annotation { "Feature Type Name" : "Feature", "Feature Type Description" : "" }
export const myFeature = defineFeature(function(context is Context, id is Id, definition is map)
    precondition{}
    {
        {
            var Q0;
            Q0=qCreatedBy(makeId("Top.planeOp"),FACE);
            var sketch = newSketch(context, id + "F0", { "sketchPlane" : qUnion([Q0])});
            skLineSegment(sketch, "E0.bottom", {"start": v(-44.45, 25.4) * mm, "end": v(44.45, 25.4) * mm});
            skLineSegment(sketch, "E0.top", {"start": v(-44.45, -25.4) * mm, "end": v(44.45, -25.4) * mm});
            skLineSegment(sketch, "E0.left", {"start": v(-44.45, 25.4) * mm, "end": v(-44.45, -25.4) * mm});
            skLineSegment(sketch, "E0.right", {"start": v(44.45, 25.4) * mm, "end": v(44.45, -25.4) * mm});
            skPoint(sketch, "E0.middle", {"position": v(0, 0) * mm});
            skSolve(sketch);
        }
        {
            var Q0;
            Q0=qSketchRegion(id+"F0",true);
            extrude(context, id + "F1", {"entities" : qUnion([Q0]), "depth" : 1.59 * mm, "offsetDistance" : 25.4 * mm});
        }
        {
            var Q0;
            {var subQ0=sQuery(id+"F0.wireOp",EDGE,"E0.right");var subQ1=sQuery(id+"F0.wireOp",EDGE,"E0.left");var subQ2=sQuery(id+"F0.wireOp",EDGE,"E0.top");var subQ3=sQuery(id+"F0.wireOp",EDGE,"E0.bottom");var subQ4=makeQuery(id+"F1.opExtrude","CAP_FACE",FACE,{"disambiguationData":[OSD([subQ3,subQ2,subQ1,subQ0])],"isStart":false});Q0=makeQuery(id+"F9.boolean.opBoolean","SPLIT",FACE,{"disambiguationData":[TD([makeQuery(id+"F5.boolean.opBoolean","COPY",FACE,{"derivedFrom":makeQuery(id+"F5.opExtrude","SWEPT_FACE",FACE,{"disambiguationData":[OSD([sQuery(id+"F4.wireOp",EDGE,"E32.sketch_text.stroke-0")])]})})])],"derivedFrom":subQ4});}
            var sketch = newSketch(context, id + "F2", { "sketchPlane" : qUnion([Q0])});
            skLineSegment(sketch, "E1", {"start": v(-39.93, 20.88) * mm, "end": v(-39.93, 13.23) * mm});
            skLineSegment(sketch, "E2", {"start": v(-39.93, 20.88) * mm, "end": v(-39.12, 20.88) * mm});
            skLineSegment(sketch, "E3", {"start": v(-37.79, -20.88) * mm, "end": v(-35.63, -20.88) * mm});
            skLineSegment(sketch, "E4.0", {"start": v(-11.09, 20.88) * mm, "end": v(-6.97, 18.68) * mm});
            skLineSegment(sketch, "E4.1", {"start": v(-14.12, 20.88) * mm, "end": v(-16.69, 18.68) * mm});
            skLineSegment(sketch, "E4.13", {"start": v(2.67, -20.88) * mm, "end": v(0.61, -18.26) * mm});
            skLineSegment(sketch, "E4.14", {"start": v(0.36, 11.02) * mm, "end": v(3.83, 4.92) * mm});
            skLineSegment(sketch, "E4.15", {"start": v(0.36, 11.02) * mm, "end": v(-4.42, 10.07) * mm});
            skArc(sketch, "E4.16", {"start": v(-4.42, 10.07) * mm, "mid": v(-5.98, 11.8) * mm, "end": v(-7.68, 13.38) * mm});
            skLineSegment(sketch, "E4.17", {"start": v(-6.97, 18.68) * mm, "end": v(-7.68, 13.38) * mm});
            skLineSegment(sketch, "E4.18", {"start": v(3.83, 4.92) * mm, "end": v(0.61, 1.3) * mm});
            skArc(sketch, "E4.19", {"start": v(1.92, -3.68) * mm, "mid": v(1.38, -1.16) * mm, "end": v(0.61, 1.3) * mm});
            skLineSegment(sketch, "E4.20", {"start": v(6.61, -5.16) * mm, "end": v(1.92, -3.68) * mm});
            skLineSegment(sketch, "E4.21", {"start": v(6.61, -5.16) * mm, "end": v(6.61, -11.77) * mm});
            skLineSegment(sketch, "E4.22", {"start": v(6.61, -11.77) * mm, "end": v(1.92, -13.28) * mm});
            skArc(sketch, "E4.23", {"start": v(0.61, -18.26) * mm, "mid": v(1.38, -15.8) * mm, "end": v(1.92, -13.28) * mm});
            skLineSegment(sketch, "E4.42", {"start": v(-39.12, 20.88) * mm, "end": v(-36.5, 18.68) * mm});
            skArc(sketch, "E4.43", {"start": v(-31.89, 19.94) * mm, "mid": v(-34.22, 19.4) * mm, "end": v(-36.5, 18.68) * mm});
            skLineSegment(sketch, "E4.44", {"start": v(-31.89, 19.94) * mm, "end": v(-31.5, 20.88) * mm});
            skLineSegment(sketch, "E4.46", {"start": v(-21.66, 20.88) * mm, "end": v(-21.3, 19.94) * mm});
            skArc(sketch, "E4.47", {"start": v(-16.69, 18.68) * mm, "mid": v(-18.96, 19.4) * mm, "end": v(-21.3, 19.94) * mm});
            skLineSegment(sketch, "E5.0", {"start": v(-17.63, -12.4) * mm, "end": v(-15.7, -16.29) * mm});
            skFitSpline(sketch, "E5.1", {"points": [v(-7.65, -15.55) * mm, v(-11.69, -15.5) * mm, v(-15.7, -16.29) * mm]});
            skLineSegment(sketch, "E5.2", {"start": v(-7.65, -15.55) * mm, "end": v(-7.5, -15.55) * mm});
            skLineSegment(sketch, "E5.3", {"start": v(-16.04, -3.68) * mm, "end": v(-14.6, -3.8) * mm});
            skFitSpline(sketch, "E5.4", {"points": [v(-14.36, -4.47) * mm, v(-14.33, -4.23) * mm, v(-14.32, -3.82) * mm, v(-14.6, -3.8) * mm]});
            skLineSegment(sketch, "E5.5", {"start": v(-14.36, -4.47) * mm, "end": v(-14.36, -7.44) * mm});
            skFitSpline(sketch, "E5.6", {"points": [v(-15.13, -7.93) * mm, v(-14.83, -7.99) * mm, v(-14.54, -8.08) * mm, v(-14.36, -7.44) * mm]});
            skFitSpline(sketch, "E5.7", {"points": [v(-16.04, -3.68) * mm, v(-16.1, 0.17) * mm, v(-19.42, 3.57) * mm, v(-23.98, 5.7) * mm, v(-24.16, 6.21) * mm]});
            skFitSpline(sketch, "E5.8", {"points": [v(-24.16, 6.21) * mm, v(-24.11, 7.19) * mm, v(-23.98, 11.28) * mm, v(-22.96, 13.3) * mm, v(-19.48, 14.97) * mm]});
            skFitSpline(sketch, "E5.9", {"points": [v(-19.48, 14.97) * mm, v(-20.81, 15.64) * mm, v(-22.46, 15.17) * mm]});
            skFitSpline(sketch, "E5.10", {"points": [v(-17.63, -12.4) * mm, v(-16.8, -10.89) * mm, v(-15.86, -9.46) * mm, v(-15.13, -7.93) * mm]});
            skFitSpline(sketch, "E5.11", {"points": [v(-22.46, 15.17) * mm, v(-21.72, 15.9) * mm, v(-20.87, 16.52) * mm]});
            skArc(sketch, "E5.12", {"start": v(-2.15, -17.45) * mm, "mid": v(-3.8, 3.8) * mm, "end": v(-20.87, 16.52) * mm});
            skLineSegment(sketch, "E5.13", {"start": v(-7.5, -15.55) * mm, "end": v(-2.15, -17.45) * mm});
            skArc(sketch, "E6.0", {"start": v(-31.1, 16.66) * mm, "mid": v(-35.68, 15.36) * mm, "end": v(-39.93, 13.23) * mm});
            skLineSegment(sketch, "E6.2", {"start": v(-38.12, -3.8) * mm, "end": v(-37.08, -3.8) * mm});
            skFitSpline(sketch, "E6.3", {"points": [v(-29.04, 5.91) * mm, v(-32.6, 3.54) * mm, v(-36.03, 3.27) * mm, v(-37.08, -3.8) * mm]});
            skFitSpline(sketch, "E6.4", {"points": [v(-32.5, 12.72) * mm, v(-29.26, 10.64) * mm, v(-29.04, 5.91) * mm]});
            skFitSpline(sketch, "E6.5", {"points": [v(-29.6, 12.07) * mm, v(-30.83, 12.9) * mm, v(-32.5, 12.72) * mm]});
            skFitSpline(sketch, "E6.6", {"points": [v(-38.12, -3.8) * mm, v(-38.46, -3.77) * mm, v(-38.6, -3.99) * mm, v(-38.6, -4.15) * mm]});
            skLineSegment(sketch, "E6.7", {"start": v(-38.6, -7.34) * mm, "end": v(-38.6, -4.15) * mm});
            skFitSpline(sketch, "E6.8", {"points": [v(-31.1, 16.66) * mm, v(-30.26, 15.3) * mm, v(-29.66, 13.77) * mm, v(-29.6, 12.07) * mm]});
            skFitSpline(sketch, "E6.9", {"points": [v(-38.6, -7.34) * mm, v(-38.84, -7.76) * mm, v(-38.04, -8) * mm]});
            skFitSpline(sketch, "E6.10", {"points": [v(-38.04, -8) * mm, v(-36.8, -10.21) * mm, v(-35.5, -12.4) * mm]});
            skLineSegment(sketch, "E6.11", {"start": v(-37.39, -16.29) * mm, "end": v(-35.5, -12.4) * mm});
            skFitSpline(sketch, "E6.12", {"points": [v(-37.39, -16.29) * mm, v(-41.55, -15.61) * mm, v(-45.73, -15.55) * mm]});
            skLineSegment(sketch, "E7.0", {"start": v(-33.08, -20.88) * mm, "end": v(-35.5, -19.2) * mm});
            skLineSegment(sketch, "E7.1", {"start": v(-35.5, -19.2) * mm, "end": v(-35.63, -20.88) * mm});
            skArc(sketch, "E8.1", {"start": v(-3.7, -20.88) * mm, "mid": v(-3.07, -19.66) * mm, "end": v(-2.52, -18.4) * mm});
            skLineSegment(sketch, "E8.2", {"start": v(-16.04, -18.26) * mm, "end": v(-15.47, -20.88) * mm});
            skFitSpline(sketch, "E8.3", {"points": [v(-16.04, -18.26) * mm, v(-16.15, -17.79) * mm, v(-15.43, -17.5) * mm]});
            skLineSegment(sketch, "E8.4", {"start": v(-7.5, -16.6) * mm, "end": v(-15.43, -17.5) * mm});
            skLineSegment(sketch, "E8.6", {"start": v(-2.52, -18.4) * mm, "end": v(-7.5, -16.6) * mm});
            skLineSegment(sketch, "E9.0", {"start": v(-37.39, -17.54) * mm, "end": v(-39.93, -17.25) * mm});
            skLineSegment(sketch, "E9.1", {"start": v(-37.79, -20.88) * mm, "end": v(-37.39, -18.92) * mm});
            skFitSpline(sketch, "E9.3", {"points": [v(-37.39, -17.54) * mm, v(-37.1, -18.3) * mm, v(-37.39, -18.92) * mm]});
            skFitSpline(sketch, "E10.0", {"points": [v(-23.19, -19.91) * mm, v(-20.18, -18.37) * mm, v(-17.6, -16.11) * mm]});
            skFitSpline(sketch, "E10.1", {"points": [v(-23.19, -19.91) * mm, v(-23.5, -19.6) * mm, v(-23.9, -19.16) * mm, v(-24.45, -18.66) * mm]});
            skFitSpline(sketch, "E10.2", {"points": [v(-17.6, -16.11) * mm, v(-17.44, -16.44) * mm, v(-17.63, -16.6) * mm]});
            skFitSpline(sketch, "E10.3", {"points": [v(-18.7, -14.2) * mm, v(-21.24, -16.8) * mm, v(-24.45, -18.66) * mm]});
            skLineSegment(sketch, "E10.4", {"start": v(-18.7, -14.2) * mm, "end": v(-18.94, -13.74) * mm});
            skFitSpline(sketch, "E10.5", {"points": [v(-17.63, -16.6) * mm, v(-19.85, -19.09) * mm, v(-22.95, -21.46) * mm, v(-27.12, -22.28) * mm, v(-31.04, -20.92) * mm, v(-33.86, -17.94) * mm, v(-35.78, -16.6) * mm]});
            skLineSegment(sketch, "E10.6", {"start": v(-34.7, -13.28) * mm, "end": v(-35.78, -16.6) * mm});
            skFitSpline(sketch, "E10.7", {"points": [v(-26.6, -18.92) * mm, v(-31.06, -16.8) * mm, v(-34.7, -13.28) * mm]});
            skFitSpline(sketch, "E10.8", {"points": [v(-18.94, -13.74) * mm, v(-21.29, -15.73) * mm, v(-23.66, -17.85) * mm, v(-26.6, -18.92) * mm]});
            skFitSpline(sketch, "E11.0", {"points": [v(-26.6, -17.54) * mm, v(-28.47, -16.2) * mm, v(-32.14, -14.27) * mm, v(-34.18, -11.66) * mm, v(-36.38, -8.05) * mm, v(-36.5, -7.34) * mm]});
            skLineSegment(sketch, "E11.1", {"start": v(-26.6, -17.54) * mm, "end": v(-24.45, -16.29) * mm});
            skFitSpline(sketch, "E11.2", {"points": [v(-26.34, -3.1) * mm, v(-21.2, -4.73) * mm, v(-16.46, -7.44) * mm]});
            skFitSpline(sketch, "E11.3", {"points": [v(-16.46, -7.44) * mm, v(-17.65, -7.44) * mm, v(-21.16, -6.55) * mm, v(-24.06, -4.55) * mm, v(-26.56, -4.47) * mm]});
            skLineSegment(sketch, "E11.4", {"start": v(-26.56, -11.18) * mm, "end": v(-26.56, -4.47) * mm});
            skFitSpline(sketch, "E11.5", {"points": [v(-36.5, -7.34) * mm, v(-33.28, -5.58) * mm, v(-29.94, -4) * mm, v(-26.34, -3.1) * mm]});
            skFitSpline(sketch, "E11.6", {"points": [v(-26.56, -11.18) * mm, v(-25.5, -14.07) * mm, v(-26.07, -15.95) * mm, v(-24.45, -16.29) * mm]});
            skFitSpline(sketch, "E12.0", {"points": [v(-29.8, -6.2) * mm, v(-28.78, -9.6) * mm, v(-28.81, -13.06) * mm]});
            skLineSegment(sketch, "E12.1", {"start": v(-28.45, -5.16) * mm, "end": v(-29.8, -6.2) * mm});
            skFitSpline(sketch, "E12.2", {"points": [v(-28.17, -12.77) * mm, v(-28.23, -8.96) * mm, v(-28.45, -5.16) * mm]});
            skFitSpline(sketch, "E12.3", {"points": [v(-28.81, -13.06) * mm, v(-28.3, -13.1) * mm, v(-28.17, -12.77) * mm]});
            skFitSpline(sketch, "E13.0", {"points": [v(-31.61, -12.77) * mm, v(-31.3, -12.82) * mm, v(-31.1, -12.4) * mm]});
            skFitSpline(sketch, "E13.1", {"points": [v(-32.64, -7.63) * mm, v(-31.76, -10.15) * mm, v(-31.61, -12.77) * mm]});
            skLineSegment(sketch, "E13.2", {"start": v(-31.61, -6.96) * mm, "end": v(-32.64, -7.63) * mm});
            skFitSpline(sketch, "E13.3", {"points": [v(-31.1, -12.4) * mm, v(-31.28, -9.67) * mm, v(-31.61, -6.96) * mm]});
            skFitSpline(sketch, "E14.0", {"points": [v(-25, -12.77) * mm, v(-24.92, -13.1) * mm, v(-24.52, -13.36) * mm, v(-23.99, -13.06) * mm]});
            skFitSpline(sketch, "E14.1", {"points": [v(-25, -12.77) * mm, v(-25.05, -9.05) * mm, v(-24.8, -5.34) * mm]});
            skLineSegment(sketch, "E14.2", {"start": v(-23.19, -6.2) * mm, "end": v(-24.8, -5.34) * mm});
            skFitSpline(sketch, "E14.3", {"points": [v(-23.99, -13.06) * mm, v(-24.35, -9.62) * mm, v(-23.19, -6.2) * mm]});
            skFitSpline(sketch, "E15.0", {"points": [v(-21.3, -12.77) * mm, v(-21.41, -12.73) * mm, v(-21.9, -12.9) * mm, v(-22.07, -12.52) * mm]});
            skFitSpline(sketch, "E15.1", {"points": [v(-21.3, -12.77) * mm, v(-21.22, -10.15) * mm, v(-20.3, -7.63) * mm]});
            skLineSegment(sketch, "E15.2", {"start": v(-20.3, -7.63) * mm, "end": v(-21.64, -6.96) * mm});
            skFitSpline(sketch, "E15.3", {"points": [v(-22.07, -12.52) * mm, v(-21.76, -9.75) * mm, v(-21.64, -6.96) * mm]});
            skFitSpline(sketch, "E16.0", {"points": [v(-27.86, -2.82) * mm, v(-31.79, -3.78) * mm, v(-35.38, -5.78) * mm]});
            skLineSegment(sketch, "E16.1", {"start": v(-27.86, -2.82) * mm, "end": v(-27.44, -1.99) * mm});
            skFitSpline(sketch, "E16.2", {"points": [v(-27.44, -1.99) * mm, v(-31.46, -2.27) * mm, v(-35.22, -4.15) * mm]});
            skFitSpline(sketch, "E16.3", {"points": [v(-35.38, -5.78) * mm, v(-35.64, -4.85) * mm, v(-35.22, -4.15) * mm]});
            skFitSpline(sketch, "E17.0", {"points": [v(-25.24, -2.82) * mm, v(-21.38, -3.85) * mm, v(-17.74, -5.62) * mm]});
            skLineSegment(sketch, "E17.1", {"start": v(-25.46, -1.99) * mm, "end": v(-25.24, -2.82) * mm});
            skFitSpline(sketch, "E17.2", {"points": [v(-17.63, -4.47) * mm, v(-21.2, -2.44) * mm, v(-25.46, -1.99) * mm]});
            skFitSpline(sketch, "E17.3", {"points": [v(-17.74, -5.62) * mm, v(-17.54, -5.08) * mm, v(-17.63, -4.47) * mm]});
            skLineSegment(sketch, "E18.0", {"start": v(-21.64, 16.53) * mm, "end": v(-21.52, 16.66) * mm});
            skArc(sketch, "E18.1", {"start": v(-21.52, 16.66) * mm, "mid": v(-22.69, 16.85) * mm, "end": v(-23.87, 17) * mm});
            skLineSegment(sketch, "E18.2", {"start": v(-23.87, 17) * mm, "end": v(-26.6, 10.84) * mm});
            skLineSegment(sketch, "E18.3", {"start": v(-26.6, 10.84) * mm, "end": v(-26.6, 17.1) * mm});
            skArc(sketch, "E18.4", {"start": v(-26.6, 17.1) * mm, "mid": v(-27.38, 17.09) * mm, "end": v(-28.17, 17.04) * mm});
            skFitSpline(sketch, "E18.5", {"points": [v(-21.64, 16.53) * mm, v(-22.97, 15.4) * mm, v(-23.04, 15.44) * mm, v(-23.74, 14.42) * mm, v(-23.43, 14.3) * mm]});
            skLineSegment(sketch, "E18.6", {"start": v(-28.17, 17.04) * mm, "end": v(-27.72, 12.88) * mm});
            skLineSegment(sketch, "E18.7", {"start": v(-26.6, 9.5) * mm, "end": v(-24.6, 6.5) * mm});
            skFitSpline(sketch, "E18.8", {"points": [v(-20.66, 14.78) * mm, v(-22.53, 14.03) * mm, v(-23.6, 12.91) * mm, v(-24.83, 10.42) * mm, v(-24.5, 8.42) * mm, v(-24.6, 6.5) * mm]});
            skFitSpline(sketch, "E18.9", {"points": [v(-23.39, 14.3) * mm, v(-22.04, 14.87) * mm, v(-20.66, 14.78) * mm]});
            skLineSegment(sketch, "E18.10", {"start": v(-23.39, 14.3) * mm, "end": v(-23.43, 14.3) * mm});
            skLineSegment(sketch, "E18.11", {"start": v(-28.64, 6.21) * mm, "end": v(-26.6, 9.5) * mm});
            skFitSpline(sketch, "E18.12", {"points": [v(-28.64, 6.21) * mm, v(-28.74, 9.43) * mm, v(-31.1, 12.15) * mm]});
            skFitSpline(sketch, "E18.13", {"points": [v(-31.1, 12.15) * mm, v(-30.03, 12.01) * mm, v(-29.04, 11.5) * mm]});
            skFitSpline(sketch, "E18.14", {"points": [v(-29.04, 11.5) * mm, v(-29.32, 14.22) * mm, v(-30.54, 16.77) * mm]});
            skArc(sketch, "E18.15", {"start": v(-29.04, 16.97) * mm, "mid": v(-29.79, 16.88) * mm, "end": v(-30.54, 16.77) * mm});
            skLineSegment(sketch, "E18.16", {"start": v(-27.72, 12.88) * mm, "end": v(-29.04, 16.97) * mm});
            skFitSpline(sketch, "E19.0", {"points": [v(-35.78, -3.1) * mm, v(-35.06, 1.3) * mm, v(-31.74, 3.25) * mm, v(-28.45, 4.52) * mm]});
            skFitSpline(sketch, "E20.0", {"points": [v(-28.45, 4.52) * mm, v(-27.52, 5.12) * mm, v(-27.11, 6.28) * mm, v(-26.6, 7.24) * mm]});
            skFitSpline(sketch, "E21.0", {"points": [v(-25.15, 4.92) * mm, v(-21.92, 3.09) * mm, v(-16.98, 0.88) * mm, v(-17.42, -3.1) * mm]});
            skFitSpline(sketch, "E21.1", {"points": [v(-26.6, 7.24) * mm, v(-25.96, 6.59) * mm, v(-25.67, 5.71) * mm, v(-25.15, 4.92) * mm]});
            skFitSpline(sketch, "E22.0", {"points": [v(-35.78, -3.1) * mm, v(-32.32, -2.55) * mm, v(-26.97, 0.08) * mm, v(-20.8, -2.33) * mm, v(-17.42, -3.1) * mm]});
            skLineSegment(sketch, "E23.trimOffspring", {"start": v(-39.93, -15.93) * mm, "end": v(-39.93, -17.25) * mm});
            skLineSegment(sketch, "E24.trimOffspring", {"start": v(-33.08, -20.88) * mm, "end": v(-30.2, -20.88) * mm});
            skFitSpline(sketch, "E25.trimOffspring", {"points": [v(-17.63, -16.6) * mm, v(-19.85, -19.09) * mm, v(-22.95, -21.46) * mm, v(-27.12, -22.28) * mm, v(-31.04, -20.92) * mm, v(-33.86, -17.94) * mm, v(-35.78, -16.6) * mm]});
            skLineSegment(sketch, "E26.trimOffspring", {"start": v(-22.9, -20.88) * mm, "end": v(-15.47, -20.88) * mm});
            skLineSegment(sketch, "E27.trimOffspring", {"start": v(-3.7, -20.88) * mm, "end": v(2.67, -20.88) * mm});
            skPoint(sketch, "E28.orphan", {"position": v(87.07, -20.88) * mm});
            skLineSegment(sketch, "E29.trimOffspring", {"start": v(-31.5, 20.88) * mm, "end": v(-21.66, 20.88) * mm});
            skPoint(sketch, "E30.orphan", {"position": v(48.02, 20.88) * mm});
            skLineSegment(sketch, "E31.trimOffspring", {"start": v(-14.12, 20.88) * mm, "end": v(-11.09, 20.88) * mm});
            skSolve(sketch);
        }
        {
            var Q0;
            Q0=qSketchRegion(id+"F2",true);
            extrude(context, id + "F3", {"entities" : qUnion([Q0]), "operationType" : NewBodyOperationType.ADD, "depth" : 0.8 * mm, "offsetDistance" : 25.4 * mm});
        }
        {
            var Q0;
            Q0=makeQuery(id+"F1.opExtrude","CAP_FACE",FACE,{"disambiguationData":[OSD([sQuery(id+"F0.wireOp",EDGE,"E0.bottom"),sQuery(id+"F0.wireOp",EDGE,"E0.top"),sQuery(id+"F0.wireOp",EDGE,"E0.left"),sQuery(id+"F0.wireOp",EDGE,"E0.right")])],"isStart":false});
            var sketch = newSketch(context, id + "F4", { "sketchPlane" : qUnion([Q0])});
            skText(sketch, "E32", { "text": "Josh Heger", "fontName": "AllertaStencil-Regular.ttf"});
            skText(sketch, "E33", { "text": "Human Player", "fontName": "AllertaStencil-Regular.ttf"});
            skText(sketch, "E34", { "text": "Team 501", "fontName": "AllertaStencil-Regular.ttf"});
            skPoint(sketch, "E35", {"position": v(0, 2.54) * mm});
            skPoint(sketch, "E36", {"position": v(0, 0) * mm});
            const initialGuessF4  = {"E32": [-0.03937, 0.0127, 1, 0, 0.00762], "E33": [-0.00956, 0.00508, 1, 0, 0.00508], "E34": [-0.01668, -0.00254, 1, 0, 0.00508]};
            skSetInitialGuess(sketch, initialGuessF4);
            skSolve(sketch);
        }
        {
            var Q0;
            Q0=qSketchRegion(id+"F4",true);
            extrude(context, id + "F5", {"entities" : qUnion([Q0]), "operationType" : NewBodyOperationType.REMOVE, "oppositeDirection" : true, "depth" : 1 / 812.8 * mm, "offsetDistance" : 25.4 * mm, "hasSecondDirection" : true, "secondDirectionOppositeDirection" : false, "secondDirectionDepth" : 25.4 * mm});
        }
        {
            var Q0;
            Q0=makeQuery(id+"F1.opExtrude","SWEPT_EDGE",EDGE,{"disambiguationData":[OSD([sQuery(id+"F0.wireOp",EDGE,"E0.bottom"),sQuery(id+"F0.wireOp",EDGE,"E0.left")])]});
            var Q1;
            Q1=makeQuery(id+"F1.opExtrude","SWEPT_EDGE",EDGE,{"disambiguationData":[OSD([sQuery(id+"F0.wireOp",EDGE,"E0.bottom"),sQuery(id+"F0.wireOp",EDGE,"E0.right")])]});
            var Q2;
            Q2=makeQuery(id+"F1.opExtrude","SWEPT_EDGE",EDGE,{"disambiguationData":[OSD([sQuery(id+"F0.wireOp",EDGE,"E0.top"),sQuery(id+"F0.wireOp",EDGE,"E0.right")])]});
            var Q3;
            Q3=makeQuery(id+"F1.opExtrude","SWEPT_EDGE",EDGE,{"disambiguationData":[OSD([sQuery(id+"F0.wireOp",EDGE,"E0.top"),sQuery(id+"F0.wireOp",EDGE,"E0.left")])]});
            fillet(context, id + "F6", {"entities" : qUnion([Q0, Q1, Q2, Q3]), "radius" : 5.08 * mm, "tangentPropagation" : true, "allowEdgeOverflow" : false});
        }
        {
            var Q0;
            Q0=makeQuery(id+"F1.opExtrude","CAP_EDGE",EDGE,{"disambiguationData":[OSD([sQuery(id+"F0.wireOp",EDGE,"E0.bottom")])],"isStart":false});
            fillet(context, id + "F7", {"entities" : qUnion([Q0]), "radius" : 5.08 * mm, "tangentPropagation" : true, "allowEdgeOverflow" : false});
        }
        {
            var Q0;
            Q0=makeQuery(id+"F1.opExtrude","CAP_FACE",FACE,{"disambiguationData":[OSD([sQuery(id+"F0.wireOp",EDGE,"E0.bottom"),sQuery(id+"F0.wireOp",EDGE,"E0.top"),sQuery(id+"F0.wireOp",EDGE,"E0.left"),sQuery(id+"F0.wireOp",EDGE,"E0.right")])],"isStart":false});
            var sketch = newSketch(context, id + "F8", { "sketchPlane" : qUnion([Q0])});
            skLineSegment(sketch, "E37", {"start": v(36.7, -11.99) * mm, "end": v(36.7, -7.33) * mm});
            skLineSegment(sketch, "E38", {"start": v(33.74, -7.33) * mm, "end": v(33.74, -10.97) * mm});
            skLineSegment(sketch, "E39", {"start": v(32.73, -11.99) * mm, "end": v(32.43, -11.99) * mm});
            skLineSegment(sketch, "E40", {"start": v(31.41, -10.97) * mm, "end": v(31.41, -7.33) * mm});
            skLineSegment(sketch, "E41", {"start": v(28.45, -7.33) * mm, "end": v(28.45, -10.97) * mm});
            skLineSegment(sketch, "E42", {"start": v(27.44, -11.99) * mm, "end": v(27.14, -11.99) * mm});
            skLineSegment(sketch, "E43", {"start": v(26.12, -10.97) * mm, "end": v(26.12, -7.33) * mm});
            skLineSegment(sketch, "E44", {"start": v(25.1, -6.31) * mm, "end": v(24.18, -6.31) * mm});
            skLineSegment(sketch, "E45", {"start": v(23.16, -7.33) * mm, "end": v(23.16, -10.97) * mm});
            skLineSegment(sketch, "E46", {"start": v(22.14, -11.99) * mm, "end": v(21.85, -11.99) * mm});
            skLineSegment(sketch, "E47", {"start": v(20.83, -10.97) * mm, "end": v(20.83, -7.33) * mm});
            skLineSegment(sketch, "E48", {"start": v(19.82, -6.31) * mm, "end": v(18.88, -6.31) * mm});
            skLineSegment(sketch, "E49", {"start": v(17.87, -7.33) * mm, "end": v(17.87, -10.97) * mm});
            skLineSegment(sketch, "E50", {"start": v(16.85, -11.99) * mm, "end": v(16.56, -11.99) * mm});
            skLineSegment(sketch, "E51", {"start": v(15.54, -10.97) * mm, "end": v(15.54, -7.33) * mm});
            skLineSegment(sketch, "E52", {"start": v(14.52, -6.31) * mm, "end": v(13.6, -6.31) * mm});
            skLineSegment(sketch, "E53", {"start": v(12.58, -7.33) * mm, "end": v(12.58, -11.99) * mm});
            skLineSegment(sketch, "E54", {"start": v(36.7, -11.99) * mm, "end": v(36.7, -17.66) * mm});
            skLineSegment(sketch, "E55", {"start": v(36.7, -17.66) * mm, "end": v(12.58, -17.66) * mm});
            skLineSegment(sketch, "E56", {"start": v(12.58, -17.66) * mm, "end": v(12.58, -11.99) * mm});
            skLineSegment(sketch, "E57", {"start": v(35.7, -6.31) * mm, "end": v(34.76, -6.31) * mm});
            skLineSegment(sketch, "E58", {"start": v(30.4, -6.31) * mm, "end": v(29.47, -6.31) * mm});
            skLineSegment(sketch, "E59", {"start": v(-40, -91.08) * mm, "end": v(-33.35, -89.42) * mm});
            skPoint(sketch, "E60.visualSharp", {"position": v(36.7, -6.31) * mm});
            skArc(sketch, "E60.filletArc", {"start": v(36.7, -7.33) * mm, "mid": v(36.4, -6.61) * mm, "end": v(35.7, -6.31) * mm});
            skPoint(sketch, "E61.visualSharp", {"position": v(33.74, -6.31) * mm});
            skArc(sketch, "E61.filletArc", {"start": v(34.76, -6.31) * mm, "mid": v(34.04, -6.61) * mm, "end": v(33.74, -7.33) * mm});
            skPoint(sketch, "E62.visualSharp", {"position": v(33.74, -11.99) * mm});
            skArc(sketch, "E62.filletArc", {"start": v(32.73, -11.99) * mm, "mid": v(33.45, -11.69) * mm, "end": v(33.74, -10.97) * mm});
            skPoint(sketch, "E63.visualSharp", {"position": v(31.41, -11.99) * mm});
            skArc(sketch, "E63.filletArc", {"start": v(31.41, -10.97) * mm, "mid": v(31.71, -11.69) * mm, "end": v(32.43, -11.99) * mm});
            skPoint(sketch, "E64.visualSharp", {"position": v(31.41, -6.31) * mm});
            skArc(sketch, "E64.filletArc", {"start": v(31.41, -7.33) * mm, "mid": v(31.12, -6.61) * mm, "end": v(30.4, -6.31) * mm});
            skPoint(sketch, "E65.visualSharp", {"position": v(28.45, -6.31) * mm});
            skArc(sketch, "E65.filletArc", {"start": v(29.47, -6.31) * mm, "mid": v(28.75, -6.61) * mm, "end": v(28.45, -7.33) * mm});
            skPoint(sketch, "E66.visualSharp", {"position": v(28.45, -11.99) * mm});
            skArc(sketch, "E66.filletArc", {"start": v(27.44, -11.99) * mm, "mid": v(28.15, -11.69) * mm, "end": v(28.45, -10.97) * mm});
            skPoint(sketch, "E67.visualSharp", {"position": v(26.12, -11.99) * mm});
            skArc(sketch, "E67.filletArc", {"start": v(26.12, -10.97) * mm, "mid": v(26.42, -11.69) * mm, "end": v(27.14, -11.99) * mm});
            skPoint(sketch, "E68.visualSharp", {"position": v(26.12, -6.31) * mm});
            skArc(sketch, "E68.filletArc", {"start": v(26.12, -7.33) * mm, "mid": v(25.83, -6.61) * mm, "end": v(25.1, -6.31) * mm});
            skPoint(sketch, "E69.visualSharp", {"position": v(23.16, -6.31) * mm});
            skArc(sketch, "E69.filletArc", {"start": v(24.18, -6.31) * mm, "mid": v(23.46, -6.61) * mm, "end": v(23.16, -7.33) * mm});
            skPoint(sketch, "E70.visualSharp", {"position": v(23.16, -11.99) * mm});
            skArc(sketch, "E70.filletArc", {"start": v(22.14, -11.99) * mm, "mid": v(22.86, -11.69) * mm, "end": v(23.16, -10.97) * mm});
            skPoint(sketch, "E71.visualSharp", {"position": v(20.83, -11.99) * mm});
            skArc(sketch, "E71.filletArc", {"start": v(20.83, -10.97) * mm, "mid": v(21.13, -11.69) * mm, "end": v(21.85, -11.99) * mm});
            skPoint(sketch, "E72.visualSharp", {"position": v(20.83, -6.31) * mm});
            skArc(sketch, "E72.filletArc", {"start": v(20.83, -7.33) * mm, "mid": v(20.53, -6.61) * mm, "end": v(19.82, -6.31) * mm});
            skPoint(sketch, "E73.visualSharp", {"position": v(17.87, -6.31) * mm});
            skArc(sketch, "E73.filletArc", {"start": v(18.88, -6.31) * mm, "mid": v(18.17, -6.61) * mm, "end": v(17.87, -7.33) * mm});
            skPoint(sketch, "E74.visualSharp", {"position": v(15.54, -6.31) * mm});
            skArc(sketch, "E74.filletArc", {"start": v(15.54, -7.33) * mm, "mid": v(15.24, -6.61) * mm, "end": v(14.52, -6.31) * mm});
            skPoint(sketch, "E75.visualSharp", {"position": v(15.54, -11.99) * mm});
            skArc(sketch, "E75.filletArc", {"start": v(15.54, -10.97) * mm, "mid": v(15.84, -11.69) * mm, "end": v(16.56, -11.99) * mm});
            skPoint(sketch, "E76.visualSharp", {"position": v(17.87, -11.99) * mm});
            skArc(sketch, "E76.filletArc", {"start": v(16.85, -11.99) * mm, "mid": v(17.57, -11.69) * mm, "end": v(17.87, -10.97) * mm});
            skPoint(sketch, "E77.visualSharp", {"position": v(12.58, -6.31) * mm});
            skArc(sketch, "E77.filletArc", {"start": v(13.6, -6.31) * mm, "mid": v(12.87, -6.61) * mm, "end": v(12.58, -7.33) * mm});
            skLineSegment(sketch, "E78.bottom", {"start": v(11.3, -20.2) * mm, "end": v(37.98, -20.2) * mm});
            skLineSegment(sketch, "E78.top", {"start": v(11.3, -3.77) * mm, "end": v(37.98, -3.77) * mm});
            skLineSegment(sketch, "E78.left", {"start": v(11.3, -20.2) * mm, "end": v(11.3, -3.77) * mm});
            skLineSegment(sketch, "E78.right", {"start": v(37.98, -20.2) * mm, "end": v(37.98, -3.77) * mm});
            skLineSegment(sketch, "E79.0", {"start": v(35.7, -7.33) * mm, "end": v(34.76, -7.33) * mm});
            skLineSegment(sketch, "E79.1", {"start": v(35.7, -11.99) * mm, "end": v(35.7, -7.33) * mm});
            skLineSegment(sketch, "E79.2", {"start": v(35.7, -11.99) * mm, "end": v(35.7, -16.64) * mm});
            skLineSegment(sketch, "E79.3", {"start": v(35.7, -16.64) * mm, "end": v(13.6, -16.64) * mm});
            skLineSegment(sketch, "E79.4", {"start": v(13.6, -16.64) * mm, "end": v(13.6, -11.99) * mm});
            skLineSegment(sketch, "E79.5", {"start": v(13.6, -7.33) * mm, "end": v(13.6, -11.99) * mm});
            skLineSegment(sketch, "E79.6", {"start": v(14.52, -7.33) * mm, "end": v(13.6, -7.33) * mm});
            skLineSegment(sketch, "E79.7", {"start": v(25.1, -10.97) * mm, "end": v(25.1, -7.33) * mm});
            skArc(sketch, "E79.8", {"start": v(25.1, -10.97) * mm, "mid": v(25.7, -12.4) * mm, "end": v(27.14, -13) * mm});
            skLineSegment(sketch, "E79.9", {"start": v(27.44, -13) * mm, "end": v(27.14, -13) * mm});
            skArc(sketch, "E79.10", {"start": v(27.44, -13) * mm, "mid": v(28.87, -12.4) * mm, "end": v(29.47, -10.97) * mm});
            skLineSegment(sketch, "E79.11", {"start": v(29.47, -7.33) * mm, "end": v(29.47, -10.97) * mm});
            skLineSegment(sketch, "E79.12", {"start": v(30.4, -7.33) * mm, "end": v(29.47, -7.33) * mm});
            skArc(sketch, "E79.13", {"start": v(32.73, -13) * mm, "mid": v(34.16, -12.4) * mm, "end": v(34.76, -10.97) * mm});
            skLineSegment(sketch, "E79.14", {"start": v(32.73, -13) * mm, "end": v(32.43, -13) * mm});
            skArc(sketch, "E79.15", {"start": v(30.4, -10.97) * mm, "mid": v(31, -12.4) * mm, "end": v(32.43, -13) * mm});
            skLineSegment(sketch, "E79.16", {"start": v(30.4, -10.97) * mm, "end": v(30.4, -7.33) * mm});
            skLineSegment(sketch, "E79.17", {"start": v(25.1, -7.33) * mm, "end": v(24.18, -7.33) * mm});
            skLineSegment(sketch, "E79.18", {"start": v(24.18, -7.33) * mm, "end": v(24.18, -10.97) * mm});
            skArc(sketch, "E79.19", {"start": v(22.14, -13) * mm, "mid": v(23.58, -12.4) * mm, "end": v(24.18, -10.97) * mm});
            skLineSegment(sketch, "E79.20", {"start": v(22.14, -13) * mm, "end": v(21.85, -13) * mm});
            skArc(sketch, "E79.21", {"start": v(19.82, -10.97) * mm, "mid": v(20.41, -12.4) * mm, "end": v(21.85, -13) * mm});
            skLineSegment(sketch, "E79.22", {"start": v(19.82, -10.97) * mm, "end": v(19.82, -7.33) * mm});
            skLineSegment(sketch, "E79.23", {"start": v(19.82, -7.33) * mm, "end": v(18.88, -7.33) * mm});
            skLineSegment(sketch, "E79.24", {"start": v(34.76, -7.33) * mm, "end": v(34.76, -10.97) * mm});
            skLineSegment(sketch, "E79.25", {"start": v(18.88, -7.33) * mm, "end": v(18.88, -10.97) * mm});
            skArc(sketch, "E79.26", {"start": v(16.85, -13) * mm, "mid": v(18.29, -12.4) * mm, "end": v(18.88, -10.97) * mm});
            skLineSegment(sketch, "E79.27", {"start": v(16.85, -13) * mm, "end": v(16.56, -13) * mm});
            skArc(sketch, "E79.28", {"start": v(14.52, -10.97) * mm, "mid": v(15.12, -12.4) * mm, "end": v(16.56, -13) * mm});
            skLineSegment(sketch, "E79.29", {"start": v(14.52, -10.97) * mm, "end": v(14.52, -7.33) * mm});
            skLineSegment(sketch, "E80.0", {"start": v(12.07, -4.54) * mm, "end": v(37.21, -4.54) * mm});
            skLineSegment(sketch, "E80.1", {"start": v(12.07, -19.44) * mm, "end": v(12.07, -4.54) * mm});
            skLineSegment(sketch, "E80.2", {"start": v(12.07, -19.44) * mm, "end": v(37.21, -19.44) * mm});
            skLineSegment(sketch, "E80.3", {"start": v(37.21, -19.44) * mm, "end": v(37.21, -4.54) * mm});
            skSolve(sketch);
        }
        {
            var Q0;
            Q0=makeQuery(id+"F8.imprint","IMPRINT",FACE,{"disambiguationData":[TD([[makeQuery(id+"F8.imprint","IMPRINT",EDGE,{"derivedFrom":sQuery(id+"F8.wireOp",EDGE,"E78.bottom")}),1.0]])]});
            var Q1;
            Q1=makeQuery(id+"F8.imprint","IMPRINT",FACE,{"disambiguationData":[TD([[makeQuery(id+"F8.imprint","IMPRINT",EDGE,{"derivedFrom":sQuery(id+"F8.wireOp",EDGE,"E37")}),1.0]])]});
            extrude(context, id + "F9", {"entities" : qUnion([Q0, Q1]), "operationType" : NewBodyOperationType.REMOVE, "oppositeDirection" : true, "depth" : 0.8 * mm, "offsetDistance" : 25.4 * mm});
        }
    });